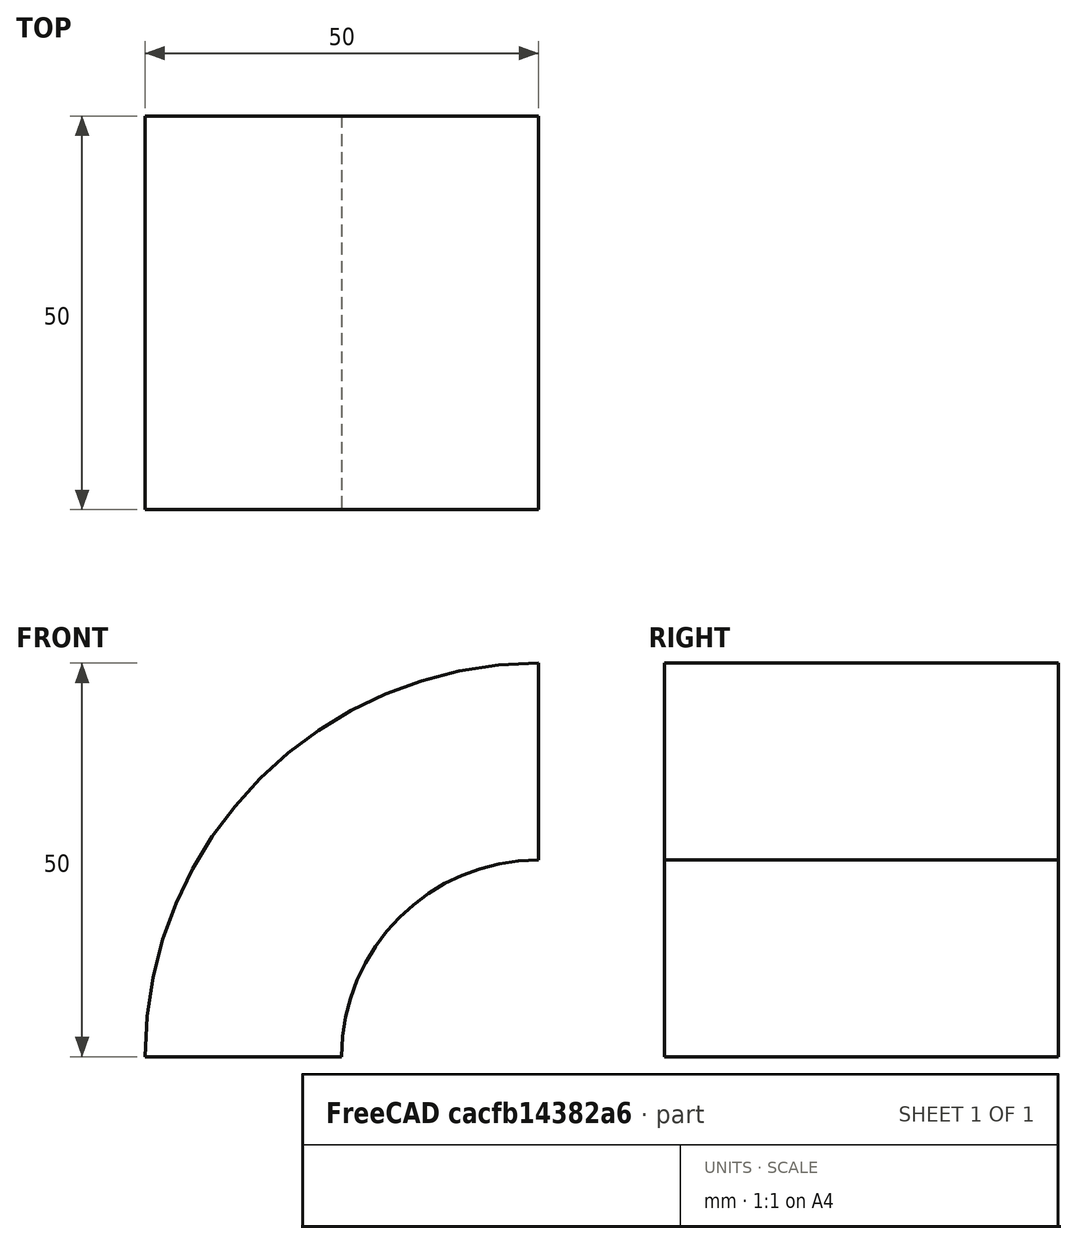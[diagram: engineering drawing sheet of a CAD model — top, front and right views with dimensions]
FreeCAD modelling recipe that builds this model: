
FCSTD DOCUMENT  (FreeCAD 1.0R39109 (Git))
Label: Half Arch
License: All rights reserved
LicenseURL: http://en.wikipedia.org/wiki/All_rights_reserved
objects: Sketcher::SketchObject×1, Spreadsheet::Sheet×1, PartDesign::Pad×1, PartDesign::Body×1
note: 6 computed .brp shape members not serialized (recipe doc carries the construction recipe); baked Part::Feature solids carry a one-line shape summary decoded from their .brp

FEATURE [Sketcher::SketchObject] Sketch
  ArcFitTolerance = 1e-06
  AttachmentSupport = -> [XZ_Plane]
  FullyConstrained = true
  MakeInternals = false
  MapMode = 5
  Placement = pos=(0,0,0) rot=(1,0,0;1.5708rad)
  expr: Constraints[10] = Spreadsheet.inner_diameter
  expr: Constraints[11] = Spreadsheet.outer_diameter
  sketch-geometry (4):
    g0: ArcOfCircle CenterX=6.1e-15 CenterY=2.14e-14 CenterZ=0 NormalX=0 NormalY=0 NormalZ=1 AngleXU=0 Radius=25 StartAngle=1.5708 EndAngle=3.14159
    g1: LineSegment StartX=6.1e-15 StartY=25 StartZ=0 EndX=6.1e-15 EndY=50 EndZ=0
    g2: LineSegment StartX=-25 StartY=2.14e-14 StartZ=0 EndX=-50 EndY=2.14e-14 EndZ=0
    g3: ArcOfCircle CenterX=6.1e-15 CenterY=2.14e-14 CenterZ=0 NormalX=0 NormalY=0 NormalZ=1 AngleXU=0 Radius=50 StartAngle=1.5708 EndAngle=3.14159
  constraints (12):
    c: Coincident(g0,g-1)
    c: Horizontal(g0,g0)
    c: Vertical(g0,g0)
    c: Coincident(g1,g0)
    c: Vertical(g1)
    c: Coincident(g2,g0)
    c: Horizontal(g2)
    c: Coincident(g3,g0)
    c: Coincident(g3,g2)
    c: Coincident(g3,g1)
    c: Diameter(g0) = 50
    c: Diameter(g3) = 100
FEATURE [Spreadsheet::Sheet] Spreadsheet
  cells = A1='inner_diameter; B1(inner_diameter)=50; A2='outer_diameter; B2(outer_diameter)=100; A3='depth; B3(depth)=50
FEATURE [PartDesign::Pad] Pad
  Direction = (0,-1,2e-16)
  Length = 50
  Length2 = 10
  Placement = pos=(0,0,0) rot=(1,0,0;1.5708rad)
  Profile = -> Sketch
  ReferenceAxis = -> Sketch [N_Axis]
  Suppressed = false
  Type = 0
  expr: Length = Spreadsheet.depth
FEATURE [PartDesign::Body] Body
  AllowCompound = false
  Group = -> [Sketch,Pad]
  Origin = -> Origin
  Tip = -> Pad
